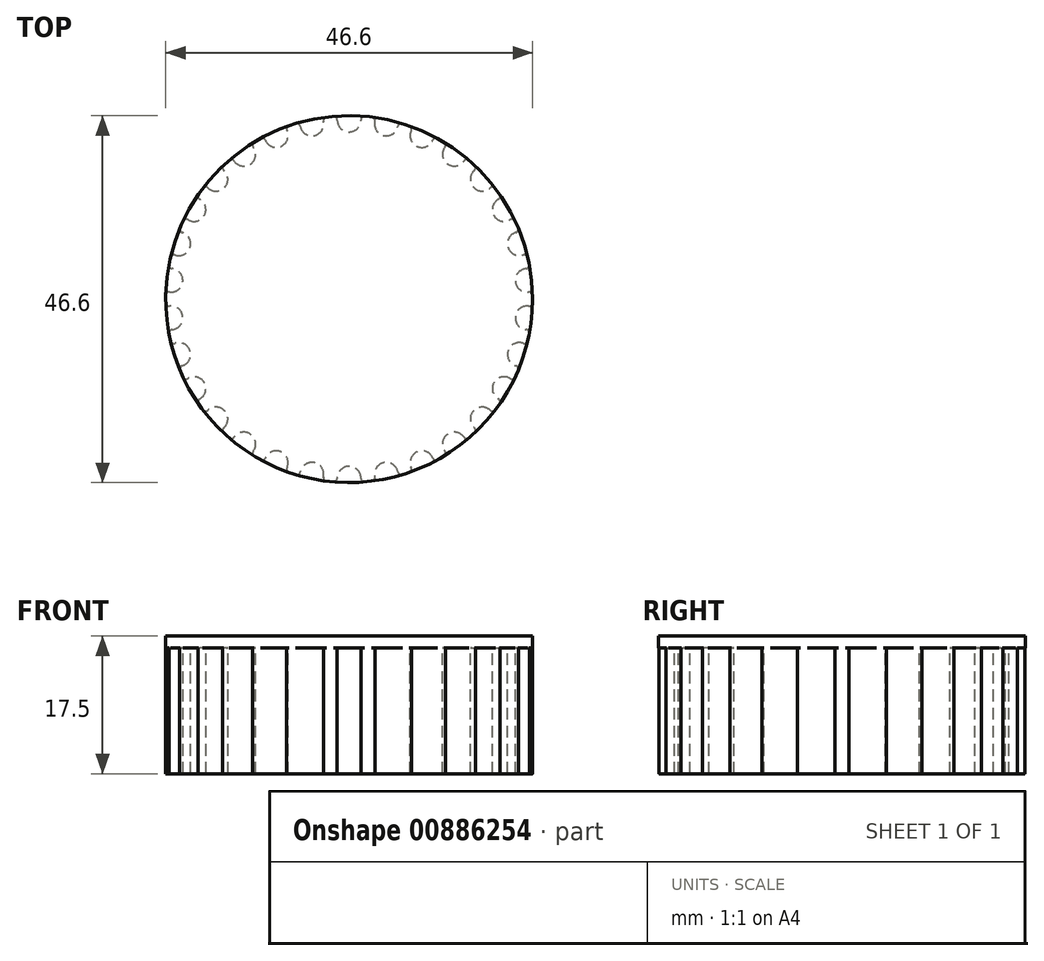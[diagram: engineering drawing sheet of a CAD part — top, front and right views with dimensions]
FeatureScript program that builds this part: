
annotation { "Feature Type Name" : "Feature", "Feature Type Description" : "" }
export const myFeature = defineFeature(function(context is Context, id is Id, definition is map)
    precondition{}
    {
        {
            assignVariable(context, id + "F0", {"name" : "Teeth", "anyValue" : 30});
        }
        {
            assignVariable(context, id + "F1", {"name" : "Width", "anyValue" : 16});
        }
        {
            var Q0;
            Q0=qCreatedBy(makeId("Top.planeOp"),FACE);
            var sketch = newSketch(context, id + "F2", { "sketchPlane" : qUnion([Q0])});
            skCircle(sketch, "E0", {"center": v(0, 0) * mm, "radius": 23.3 * mm});
            skSolve(sketch);
        }
        {
            var Q0;
            Q0=qSketchRegion(id+"F2",true);
            extrude(context, id + "F3", {"entities" : qUnion([Q0]), "depth" : (getVariable(context, 'Width')) * mm});
        }
        {
            var Q0;
            Q0=makeQuery(id+"F3.opExtrude","CAP_FACE",FACE,{"disambiguationData":[OSD([sQuery(id+"F2.wireOp",EDGE,"E0")])],"isStart":false});
            var sketch = newSketch(context, id + "F4", { "sketchPlane" : qUnion([Q0])});
            skCircle(sketch, "E1", {"center": v(0, 0) * mm, "radius": 21.24 * mm, "construction": true});
            skArc(sketch, "E2", {"start": v(-1.5, 22.76) * mm, "mid": v(0, 21.24) * mm, "end": v(1.5, 22.76) * mm});
            skArc(sketch, "E3", {"start": v(1.99, 23.22) * mm, "mid": v(0, 23.3) * mm, "end": v(-1.99, 23.22) * mm});
            skArc(sketch, "E4", {"start": v(-1.5, 22.76) * mm, "mid": v(-1.64, 23.1) * mm, "end": v(-1.99, 23.22) * mm});
            skArc(sketch, "E5", {"start": v(1.99, 23.22) * mm, "mid": v(1.64, 23.1) * mm, "end": v(1.5, 22.76) * mm});
            skSolve(sketch);
        }
        {
            var Q0;
            Q0=makeQuery(id+"F4.imprint","IMPRINT",FACE,{"disambiguationData":[TD([[makeQuery(id+"F4.imprint","IMPRINT",EDGE,{"derivedFrom":sQuery(id+"F4.wireOp",EDGE,"E2")}),1.0]])]});
            var Q1;
            Q1=makeQuery(id+"F3.opExtrude","CAP_FACE",FACE,{"disambiguationData":[OSD([sQuery(id+"F2.wireOp",EDGE,"E0")])],"isStart":true});
            extrude(context, id + "F5", {"entities" : qUnion([Q0]), "operationType" : NewBodyOperationType.REMOVE, "endBound" : BoundingType.UP_TO_SURFACE, "oppositeDirection" : true, "endBoundEntityFace" : qUnion([Q1]), "depth" : 25 * mm});
        }
        {
            var Q0;
            Q0=makeQuery(id+"F5.boolean.opBoolean","COPY",FACE,{"derivedFrom":makeQuery(id+"F5.opExtrude","SWEPT_FACE",FACE,{"disambiguationData":[OSD([sQuery(id+"F4.wireOp",EDGE,"E4")])]})});
            var Q1;
            Q1=makeQuery(id+"F5.boolean.opBoolean","COPY",FACE,{"derivedFrom":makeQuery(id+"F5.opExtrude","SWEPT_FACE",FACE,{"disambiguationData":[OSD([sQuery(id+"F4.wireOp",EDGE,"kHu0Iwj9-o4Cv-DRlk-4OjM-lw9Y4UkXsprA")])]})});
            var Q2;
            Q2=makeQuery(id+"F5.boolean.opBoolean","COPY",FACE,{"derivedFrom":makeQuery(id+"F5.opExtrude","SWEPT_FACE",FACE,{"disambiguationData":[OSD([sQuery(id+"F4.wireOp",EDGE,"E2")])]})});
            var Q3;
            Q3=makeQuery(id+"F5.boolean.opBoolean","COPY",FACE,{"derivedFrom":makeQuery(id+"F5.opExtrude","SWEPT_FACE",FACE,{"disambiguationData":[OSD([sQuery(id+"F4.wireOp",EDGE,"lCBZwTSR-BtAH-iuKv-YoZ4-wjcx4KIexOll")])]})});
            var Q4;
            Q4=makeQuery(id+"F5.boolean.opBoolean","COPY",FACE,{"derivedFrom":makeQuery(id+"F5.opExtrude","SWEPT_FACE",FACE,{"disambiguationData":[OSD([sQuery(id+"F4.wireOp",EDGE,"E5")])]})});
            var Q5;
            Q5=makeQuery(id+"F3.opExtrude","SWEPT_FACE",FACE,{"disambiguationData":[OSD([sQuery(id+"F2.wireOp",EDGE,"E0")])]});
            circularPattern(context, id + "F6", {"faces" : qUnion([Q0, Q1, Q2, Q3, Q4]), "axis" : qUnion([Q5]), "angle" : 360 * degree, "instanceCount" : getVariable(context, 'Teeth'), "equalSpace" : true, "patternType" : PatternType.FACE});
        }
        {
            var Q0;
            Q0=makeQuery(id+"F3.opExtrude","CAP_FACE",FACE,{"disambiguationData":[OSD([sQuery(id+"F2.wireOp",EDGE,"E0")])],"isStart":false});
            var sketch = newSketch(context, id + "F7", { "sketchPlane" : qUnion([Q0])});
            skCircle(sketch, "E6.0", {"center": v(0, 0) * mm, "radius": 23.3 * mm});
            skSolve(sketch);
        }
        {
            var Q0;
            Q0=qSketchRegion(id+"F7",true);
            extrude(context, id + "F8", {"entities" : qUnion([Q0]), "operationType" : NewBodyOperationType.ADD, "depth" : 1.5 * mm});
        }
    });
